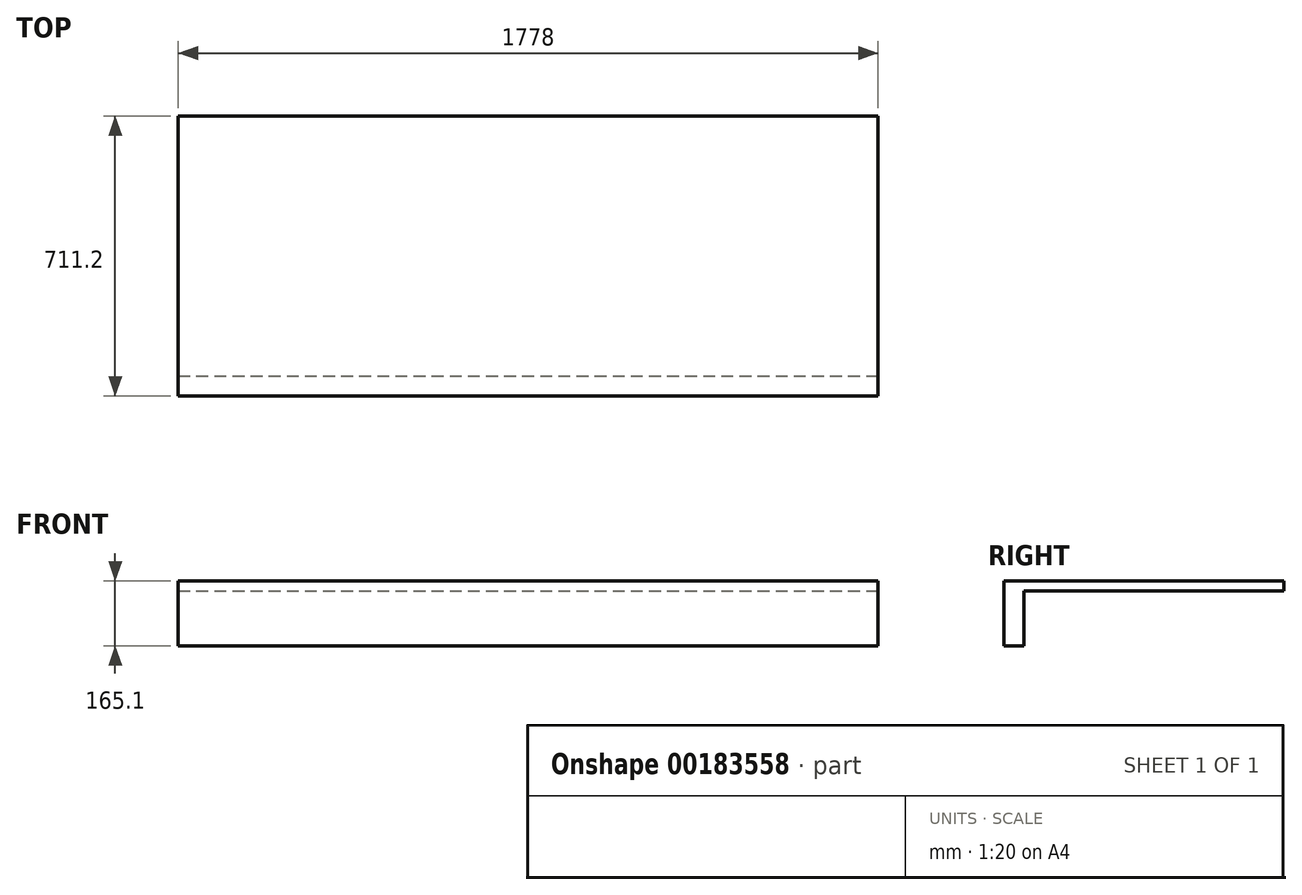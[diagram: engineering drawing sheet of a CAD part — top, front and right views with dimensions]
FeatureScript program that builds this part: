
annotation { "Feature Type Name" : "Feature", "Feature Type Description" : "" }
export const myFeature = defineFeature(function(context is Context, id is Id, definition is map)
    precondition{}
    {
        {
            var Q0;
            Q0=qCreatedBy(makeId("Top.planeOp"),FACE);
            var sketch = newSketch(context, id + "F0", { "sketchPlane" : qUnion([Q0])});
            skLineSegment(sketch, "E0.bottom", {"start": v(-889, 355.6) * mm, "end": v(889, 355.6) * mm});
            skLineSegment(sketch, "E0.top", {"start": v(-889, -355.6) * mm, "end": v(889, -355.6) * mm});
            skLineSegment(sketch, "E0.left", {"start": v(-889, 355.6) * mm, "end": v(-889, -355.6) * mm});
            skLineSegment(sketch, "E0.right", {"start": v(889, 355.6) * mm, "end": v(889, -355.6) * mm});
            skPoint(sketch, "E0.middle", {"position": v(0, 0) * mm});
            skSolve(sketch);
        }
        {
            var Q0;
            Q0=makeQuery(id+"F0.imprint","IMPRINT",FACE,{"disambiguationData":[TD([[makeQuery(id+"F0.imprint","IMPRINT",EDGE,{"derivedFrom":sQuery(id+"F0.wireOp",EDGE,"E0.bottom")}),-1.0]])]});
            extrude(context, id + "F1", {"entities" : qUnion([Q0]), "depth" : 25.4 * mm});
        }
        {
            var Q0;
            Q0=makeQuery(id+"F1.opExtrude","CAP_FACE",FACE,{"disambiguationData":[OSD([sQuery(id+"F0.wireOp",EDGE,"E0.bottom"),sQuery(id+"F0.wireOp",EDGE,"E0.top"),sQuery(id+"F0.wireOp",EDGE,"E0.left"),sQuery(id+"F0.wireOp",EDGE,"E0.right")])],"isStart":true});
            var sketch = newSketch(context, id + "F2", { "sketchPlane" : qUnion([Q0])});
            skLineSegment(sketch, "E1.bottom", {"start": v(-889, 355.6) * mm, "end": v(889, 355.6) * mm});
            skLineSegment(sketch, "E1.top", {"start": v(-889, 304.8) * mm, "end": v(889, 304.8) * mm});
            skLineSegment(sketch, "E1.left", {"start": v(-889, 355.6) * mm, "end": v(-889, 304.8) * mm});
            skLineSegment(sketch, "E1.right", {"start": v(889, 355.6) * mm, "end": v(889, 304.8) * mm});
            skSolve(sketch);
        }
        {
            var Q0;
            Q0 = qSketchRegion(id + "F2", true);
            extrude(context, id + "F3", {"entities" : qUnion([Q0]), "operationType" : NewBodyOperationType.ADD, "depth" : 139.7 * mm});
        }
    });
